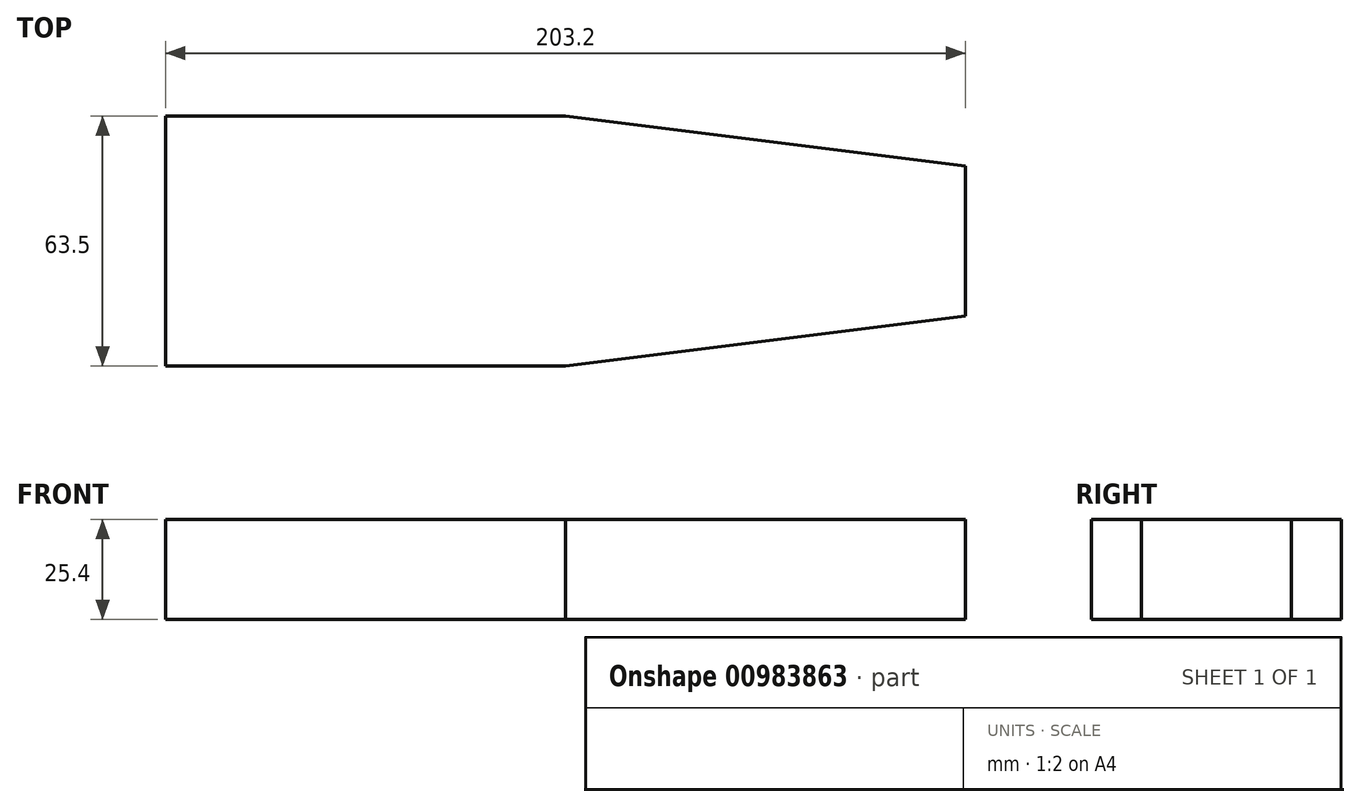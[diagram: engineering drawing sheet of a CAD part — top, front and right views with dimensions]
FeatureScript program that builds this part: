
annotation { "Feature Type Name" : "Feature", "Feature Type Description" : "" }
export const myFeature = defineFeature(function(context is Context, id is Id, definition is map)
    precondition{}
    {
        {
            var Q0;
            Q0=qCreatedBy(makeId("Top.planeOp"),FACE);
            var sketch = newSketch(context, id + "F0", { "sketchPlane" : qUnion([Q0])});
            skLineSegment(sketch, "E0.bottom", {"start": v(-101.6, 31.75) * mm, "end": v(0, 31.75) * mm});
            skLineSegment(sketch, "E0.top", {"start": v(-101.6, -31.75) * mm, "end": v(0, -31.75) * mm});
            skLineSegment(sketch, "E0.left", {"start": v(-101.6, 31.75) * mm, "end": v(-101.6, -31.75) * mm});
            skLineSegment(sketch, "E1", {"start": v(0, -31.75) * mm, "end": v(101.6, -19.05) * mm});
            skLineSegment(sketch, "E2", {"start": v(101.6, 19.05) * mm, "end": v(0, 31.75) * mm});
            skLineSegment(sketch, "E3", {"start": v(101.6, -19.05) * mm, "end": v(101.6, 0) * mm});
            skLineSegment(sketch, "E4", {"start": v(101.6, 0) * mm, "end": v(101.6, 19.05) * mm});
            skSolve(sketch);
        }
        {
            var Q0;
            Q0 = qSketchRegion(id + "F0", true);
            extrude(context, id + "F1", {"entities" : qUnion([Q0]), "depth" : 25.4 * mm, "offsetDistance" : 25.4 * mm});
        }
    });
